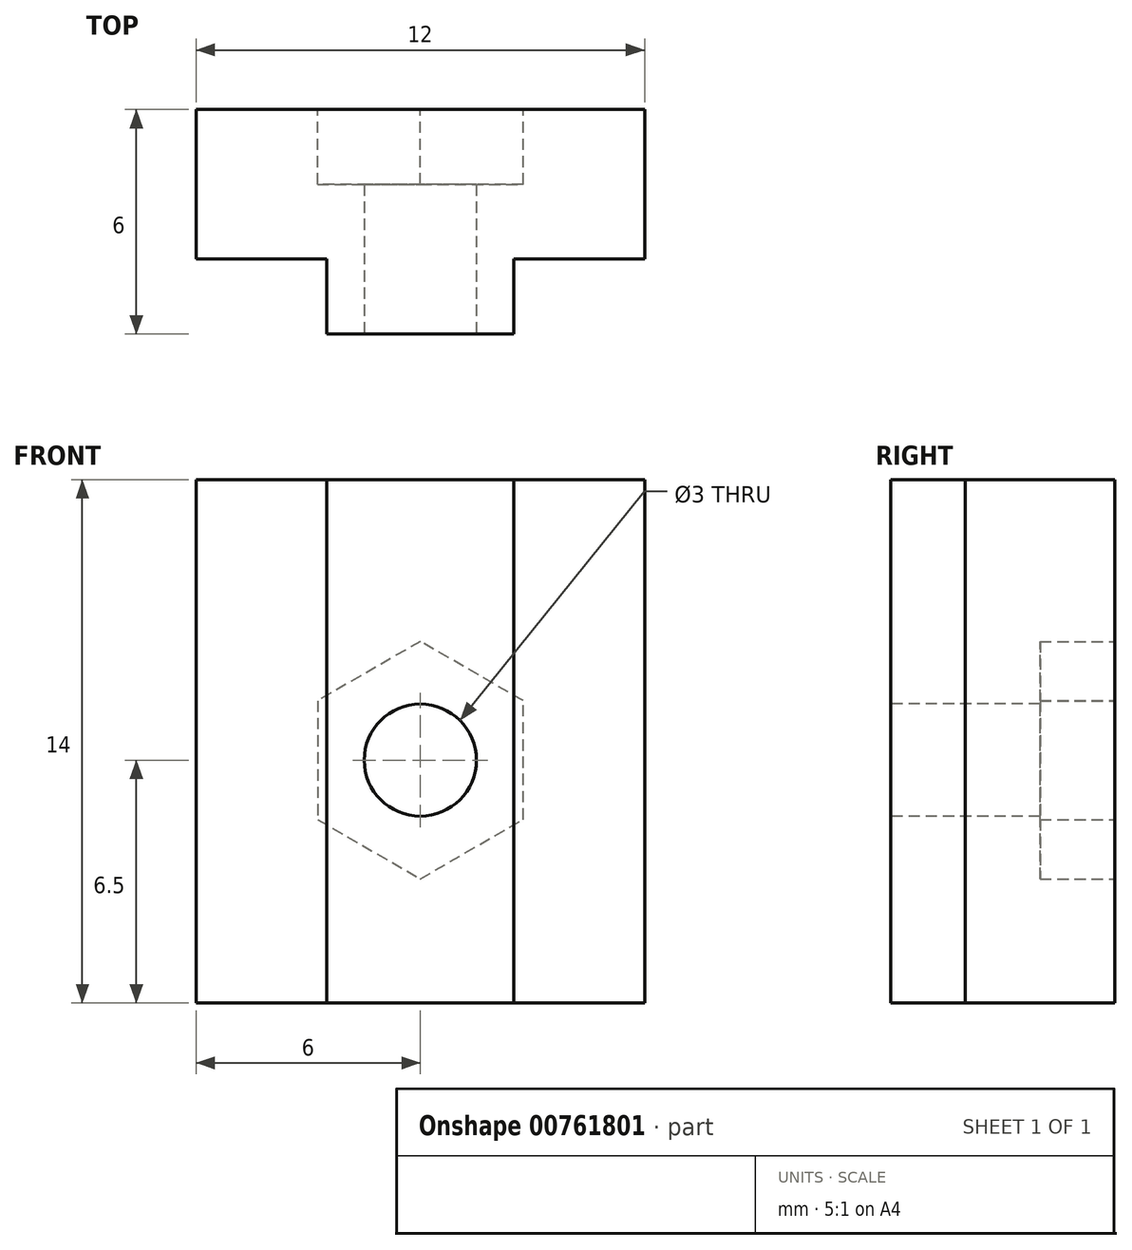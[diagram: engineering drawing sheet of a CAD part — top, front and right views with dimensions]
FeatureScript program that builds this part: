
annotation { "Feature Type Name" : "Feature", "Feature Type Description" : "" }
export const myFeature = defineFeature(function(context is Context, id is Id, definition is map)
    precondition{}
    {
        {
            var Q0;
            Q0=qCreatedBy(makeId("Front.planeOp"),FACE);
            var sketch = newSketch(context, id + "F0", { "sketchPlane" : qUnion([Q0])});
            skLineSegment(sketch, "E0.bottom", {"start": v(6, -20) * mm, "end": v(-6, -20) * mm});
            skLineSegment(sketch, "E0.top", {"start": v(6, 20) * mm, "end": v(-6, 20) * mm});
            skLineSegment(sketch, "E0.left", {"start": v(6, -20) * mm, "end": v(6, 20) * mm});
            skLineSegment(sketch, "E0.right", {"start": v(-6, -20) * mm, "end": v(-6, 20) * mm});
            skPoint(sketch, "E0.middle", {"position": v(0, 0) * mm});
            skSolve(sketch);
        }
        {
            var Q0;
            Q0=makeQuery(id+"F0.imprint","IMPRINT",FACE,{"disambiguationData":[TD([[makeQuery(id+"F0.imprint","IMPRINT",EDGE,{"derivedFrom":sQuery(id+"F0.wireOp",EDGE,"E0.bottom")}),-1.0]])]});
            extrude(context, id + "F1", {"entities" : qUnion([Q0]), "depth" : 4 * mm, "offsetDistance" : 25 * mm});
        }
        {
            var Q0;
            Q0=makeQuery(id+"F1.opExtrude","CAP_FACE",FACE,{"disambiguationData":[OSD([sQuery(id+"F0.wireOp",EDGE,"E0.bottom"),sQuery(id+"F0.wireOp",EDGE,"E0.top"),sQuery(id+"F0.wireOp",EDGE,"E0.left"),sQuery(id+"F0.wireOp",EDGE,"E0.right")])],"isStart":false});
            var sketch = newSketch(context, id + "F2", { "sketchPlane" : qUnion([Q0])});
            skLineSegment(sketch, "E1.bottom", {"start": v(2.5, -20) * mm, "end": v(-2.5, -20) * mm});
            skLineSegment(sketch, "E1.top", {"start": v(2.5, 20) * mm, "end": v(-2.5, 20) * mm});
            skLineSegment(sketch, "E1.left", {"start": v(2.5, -20) * mm, "end": v(2.5, 20) * mm});
            skLineSegment(sketch, "E1.right", {"start": v(-2.5, -20) * mm, "end": v(-2.5, 20) * mm});
            skPoint(sketch, "E1.middle", {"position": v(0, 0) * mm});
            skSolve(sketch);
        }
        {
            var Q0;
            Q0 = qSketchRegion(id + "F2", true);
            extrude(context, id + "F3", {"entities" : qUnion([Q0]), "operationType" : NewBodyOperationType.ADD, "depth" : 2 * mm, "offsetDistance" : 25 * mm});
        }
        {
            var Q0;
            Q0=makeQuery(id+"F3.opExtrude","CAP_FACE",FACE,{"disambiguationData":[OSD([sQuery(id+"F2.wireOp",EDGE,"E1.bottom"),sQuery(id+"F2.wireOp",EDGE,"E1.top"),sQuery(id+"F2.wireOp",EDGE,"E1.left"),sQuery(id+"F2.wireOp",EDGE,"E1.right")])],"isStart":false});
            var sketch = newSketch(context, id + "F4", { "sketchPlane" : qUnion([Q0])});
            skCircle(sketch, "E2", {"center": v(0, 16.5) * mm, "radius": 1.5 * mm});
            skCircle(sketch, "E3", {"center": v(0, -13.5) * mm, "radius": 1.5 * mm});
            skSolve(sketch);
        }
        {
            var Q0;
            Q0 = qSketchRegion(id + "F4", true);
            extrude(context, id + "F5", {"entities" : qUnion([Q0]), "operationType" : NewBodyOperationType.REMOVE, "oppositeDirection" : true, "depth" : 25 * mm, "offsetDistance" : 25 * mm});
        }
        {
            var Q0;
            Q0=makeQuery(id+"F1.opExtrude","CAP_FACE",FACE,{"disambiguationData":[OSD([sQuery(id+"F0.wireOp",EDGE,"E0.bottom"),sQuery(id+"F0.wireOp",EDGE,"E0.top"),sQuery(id+"F0.wireOp",EDGE,"E0.left"),sQuery(id+"F0.wireOp",EDGE,"E0.right")])],"isStart":true});
            var sketch = newSketch(context, id + "F6", { "sketchPlane" : qUnion([Q0])});
            skCircle(sketch, "E4.cCircle", {"center": v(0, 16.5) * mm, "radius": 2.75 * mm, "construction": true});
            skLineSegment(sketch, "E4.0", {"start": v(2.75, 18.09) * mm, "end": v(2.75, 14.91) * mm});
            skLineSegment(sketch, "E4.1", {"start": v(2.75, 14.91) * mm, "end": v(0, 13.32) * mm});
            skLineSegment(sketch, "E4.2", {"start": v(0, 13.32) * mm, "end": v(-2.75, 14.91) * mm});
            skLineSegment(sketch, "E4.3", {"start": v(-2.75, 14.91) * mm, "end": v(-2.75, 18.09) * mm});
            skLineSegment(sketch, "E4.4", {"start": v(-2.75, 18.09) * mm, "end": v(0, 19.68) * mm});
            skLineSegment(sketch, "E4.5", {"start": v(0, 19.68) * mm, "end": v(2.75, 18.09) * mm});
            skPoint(sketch, "E4.0.midPoint", {"position": v(2.75, 16.5) * mm});
            skCircle(sketch, "E5.cCircle", {"center": v(0, -13.5) * mm, "radius": 2.75 * mm, "construction": true});
            skLineSegment(sketch, "E5.0", {"start": v(0, -10.32) * mm, "end": v(2.75, -11.91) * mm});
            skLineSegment(sketch, "E5.1", {"start": v(2.75, -11.91) * mm, "end": v(2.75, -15.09) * mm});
            skLineSegment(sketch, "E5.2", {"start": v(2.75, -15.09) * mm, "end": v(0, -16.68) * mm});
            skLineSegment(sketch, "E5.3", {"start": v(0, -16.68) * mm, "end": v(-2.75, -15.09) * mm});
            skLineSegment(sketch, "E5.4", {"start": v(-2.75, -15.09) * mm, "end": v(-2.75, -11.91) * mm});
            skLineSegment(sketch, "E5.5", {"start": v(-2.75, -11.91) * mm, "end": v(0, -10.32) * mm});
            skPoint(sketch, "E5.0.midPoint", {"position": v(1.38, -11.12) * mm});
            skSolve(sketch);
        }
        {
            var Q0;
            Q0=makeQuery(id+"F6.imprint","IMPRINT",FACE,{"disambiguationData":[TD([[makeQuery(id+"F6.imprint","IMPRINT",EDGE,{"derivedFrom":sQuery(id+"F6.wireOp",EDGE,"E4.0")}),-1.0]])]});
            var Q1;
            Q1=makeQuery(id+"F6.imprint","IMPRINT",FACE,{"disambiguationData":[TD([[makeQuery(id+"F6.imprint","IMPRINT",EDGE,{"derivedFrom":sQuery(id+"F6.wireOp",EDGE,"E5.0")}),-1.0]])]});
            extrude(context, id + "F7", {"entities" : qUnion([Q0, Q1]), "operationType" : NewBodyOperationType.REMOVE, "oppositeDirection" : true, "depth" : 2 * mm, "offsetDistance" : 25 * mm});
        }
        {
            var Q0;
            Q0=makeQuery(id+"F1.opExtrude","CAP_FACE",FACE,{"disambiguationData":[OSD([sQuery(id+"F0.wireOp",EDGE,"E0.bottom"),sQuery(id+"F0.wireOp",EDGE,"E0.top"),sQuery(id+"F0.wireOp",EDGE,"E0.left"),sQuery(id+"F0.wireOp",EDGE,"E0.right")])],"isStart":true});
            var sketch = newSketch(context, id + "F8", { "sketchPlane" : qUnion([Q0])});
            skLineSegment(sketch, "E6.bottom", {"start": v(-6, 20) * mm, "end": v(10.03, 20) * mm});
            skLineSegment(sketch, "E6.top", {"start": v(-6, -6) * mm, "end": v(10.03, -6) * mm});
            skLineSegment(sketch, "E6.left", {"start": v(-6, 20) * mm, "end": v(-6, -6) * mm});
            skLineSegment(sketch, "E6.right", {"start": v(10.03, 20) * mm, "end": v(10.03, -6) * mm});
            skSolve(sketch);
        }
        {
            var Q0;
            {var subQ3=sQuery(id+"F8.wireOp",EDGE,"E6.right");Q0=makeQuery(id+"F8.imprint","IMPRINT",FACE,{"disambiguationData":[TD([[makeQuery(id+"F8.imprint","IMPRINT",EDGE,{"derivedFrom":subQ3}),-1.0]])]});}
            var Q1;
            {var subQ0=sQuery(id+"F8.wireOp",EDGE,"E6.left");Q1=makeQuery(id+"F8.imprint","IMPRINT",FACE,{"disambiguationData":[TD([[makeQuery(id+"F8.imprint","IMPRINT",EDGE,{"derivedFrom":subQ0}),-1.0]])]});}
            var Q2;
            Q2=makeQuery(id+"F8.imprint","IMPRINT",FACE,{"disambiguationData":[TD([[makeQuery(id+"F8.imprint","IMPRINT",EDGE,{"derivedFrom":makeQuery(id+"F7.boolean.opBoolean","COPY",EDGE,{"derivedFrom":makeQuery(id+"F7.opExtrude","CAP_EDGE",EDGE,{"disambiguationData":[OSD([sQuery(id+"F6.wireOp",EDGE,"E4.0")])],"isStart":true})})}),-1.0]])]});
            extrude(context, id + "F9", {"entities" : qUnion([Q0, Q1, Q2]), "operationType" : NewBodyOperationType.REMOVE, "oppositeDirection" : true, "depth" : 25 * mm, "offsetDistance" : 25 * mm});
        }
    });
